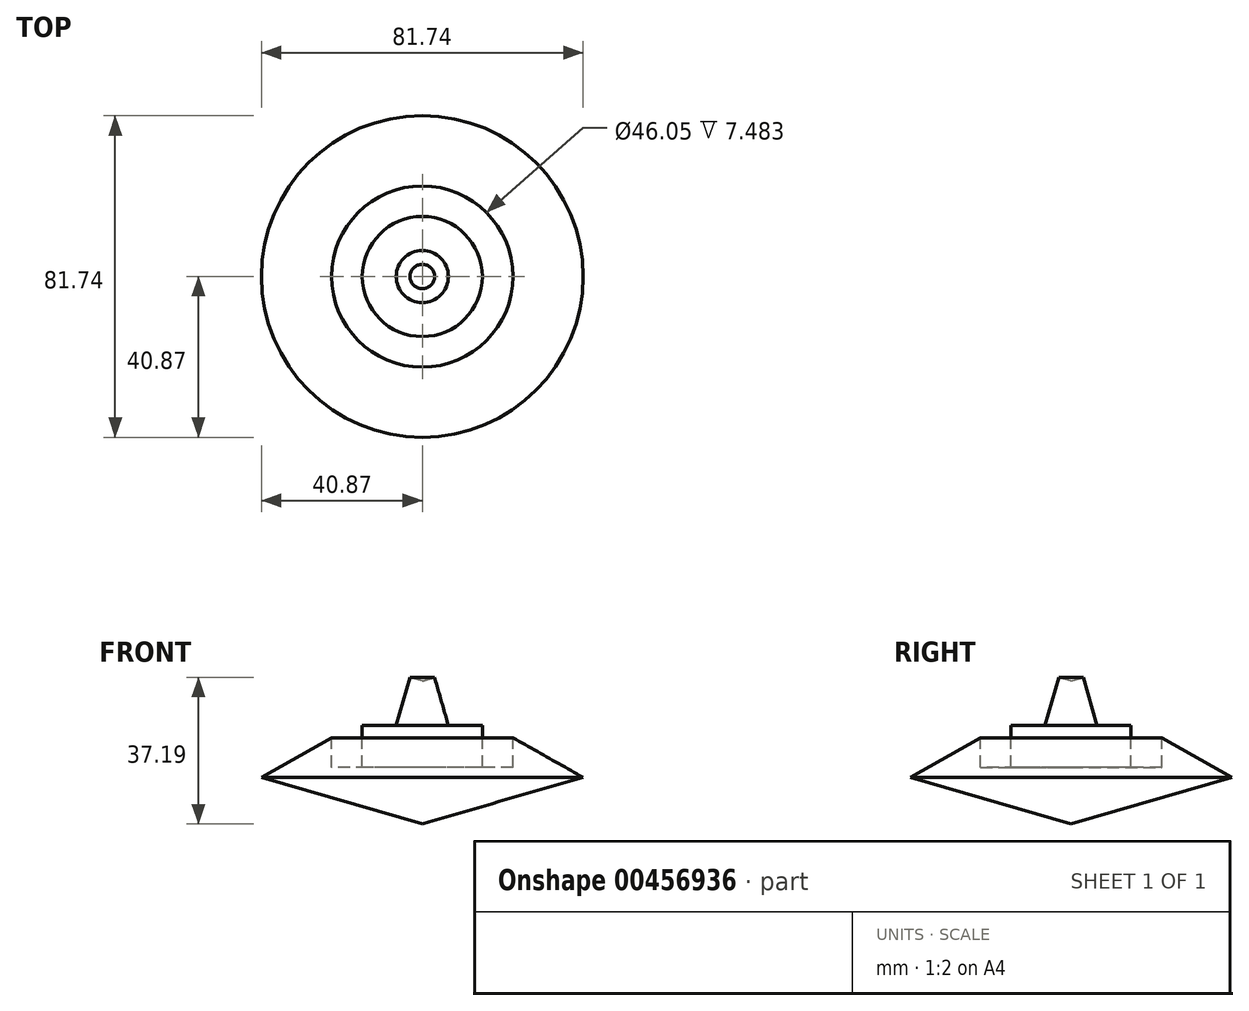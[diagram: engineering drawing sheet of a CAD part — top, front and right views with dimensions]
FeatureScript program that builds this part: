
annotation { "Feature Type Name" : "Feature", "Feature Type Description" : "" }
export const myFeature = defineFeature(function(context is Context, id is Id, definition is map)
    precondition{}
    {
        {
            var Q0;
            Q0=qCreatedBy(makeId("Front.planeOp"),FACE);
            var sketch = newSketch(context, id + "F0", { "sketchPlane" : qUnion([Q0])});
            skLineSegment(sketch, "E0", {"start": v(0, 0) * mm, "end": v(40.87, 11.8) * mm});
            skLineSegment(sketch, "E1", {"start": v(40.87, 11.8) * mm, "end": v(23.02, 21.87) * mm});
            skLineSegment(sketch, "E2", {"start": v(23.02, 21.87) * mm, "end": v(23.02, 14.4) * mm});
            skLineSegment(sketch, "E3", {"start": v(23.02, 14.4) * mm, "end": v(15.25, 14.4) * mm});
            skLineSegment(sketch, "E4", {"start": v(15.25, 14.4) * mm, "end": v(15.25, 25.04) * mm});
            skLineSegment(sketch, "E5", {"start": v(15.25, 25.04) * mm, "end": v(6.62, 25.04) * mm});
            skLineSegment(sketch, "E6", {"start": v(6.62, 25.04) * mm, "end": v(3.11, 37.19) * mm});
            skLineSegment(sketch, "E7", {"start": v(3.11, 37.19) * mm, "end": v(0, 36.29) * mm});
            skLineSegment(sketch, "E8", {"start": v(0, 36.29) * mm, "end": v(0, 0) * mm});
            skSolve(sketch);
        }
        {
            var Q0;
            Q0=makeQuery(id+"F0.imprint","IMPRINT",FACE,{"disambiguationData":[TD([[makeQuery(id+"F0.imprint","IMPRINT",EDGE,{"derivedFrom":sQuery(id+"F0.wireOp",EDGE,"E0")}),1.0]])]});
            var Q1;
            Q1=sQuery(id+"F0.wireOp",EDGE,"E8");
            revolve(context, id + "F1", {"entities" : qUnion([Q0]), "axis" : qUnion([Q1]), "revolveType" : RevolveType.FULL});
        }
    });
